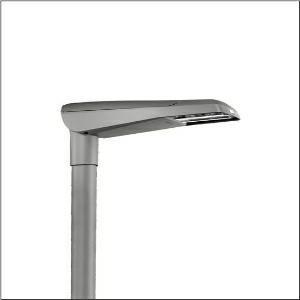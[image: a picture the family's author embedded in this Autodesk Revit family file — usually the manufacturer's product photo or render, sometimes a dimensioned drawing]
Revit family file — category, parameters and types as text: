
# Revit family: streetlight_sl_11_iq_micro___st1_2a_5xc1a51e08ce_3341
name_source: partatom
category: Lighting Fixtures
units: mm (PartAtom-declared; Revit-internal decimal feet)

## family parameters
Cut with Voids When Loaded = No
Host = Face
Light Source = No
Part Type = Normal
Room Calculation Point = No
Round Connector Dimension = Use Diameter
Shared = No

## types (1)
- --- (1 x LED, 1880 lm, 12.6 W, 3000K)
    Apparent Load = 13 VA
    CIE Flux Codes = 33 71 96 100 100
    Color Rendering = 70
    Color Temperature = 3000K
    Default Elevation = 1800 mm
    Description = Streetlight SL 11 iQ micro, mast luminaire, primary light control with 3 zone facetted reflector, of plastic, silver coated, highly specular, primary optical cover: cover, of PMMA, transparent, light distribution: ST1.2a, light emission: direct distribution, primary light characteristic: asymmetric, installation type: post-top, side-entry, lamps: LED, High Power LED, rated values: 1.880lm | 12,6W | 149,2lm/W (begin service life); end service life: 1.880lm | 12,9W; at 50% lumin. flux: 940lm | 6,8W | 138,2lm/W, colour temperature: 3000K, colour rendering: CRI > 70, light colour: 730, light setting 1 begin service life: 100% | 1.880lm | 12,6W | 149,2lm/W | 3.000K, light setting 1 end service life: 12,9W, further light settings possible, control: optimised constant luminous flux control (CLO 2.0), Desk-Remote (wireless, voltage-free reading and setting of iQ features in the workshop via application-optimized NFC function/RFID function), Light-Fading, Smart-Wire, Night-Set, Lumen-Switch, Temp-Guard, Auto-Match, with cable H07RN-F 3x 1.5mm², mains connection: 230..240V, AC, 50/60Hz, connection cable pre-assembled, cable length: 5,5m, luminaire housing, of diecast aluminium, powder-coated, SITECO metallic grey (DB 702S), please order mast flange separately, inclination adjustable without tools: 0°, 5°, 10°, 15° (post-top) | 0°, -5°, -10°, -15° (side-entry), sealing non-destructively replaceable, multi-level sealing system, length: 600mm, width: 174mm, height: 116mm, mast flange for spigot size: 42mm (side-entry): 5XC10008XM4, 60/48mm (side-entry/post-top): 5XC10108XM2, 76/60mm (side-entry/post-top): 5XC10108XM1, equipment: standard, protection rating (complete): IP66, insulation class (complete): insulation class II (safety insulation), certification: CE, ENEC, ENEC+, VDE, impact resistance: IK10, permissible operating ambient temperature for outdoor applications: -25..+50°C, standard-compliant lighting for roads and squares, Environmental Product Declaration (EPD) tested and certified by an independent institute, packaging unit: 1 piece

Light Distribution: ST1.2a
    Height = 116 mm
    Lamp = 1 x LED
    Lamp Light Flux = 1880 lm
    Lamp Power = 12.6 W
    Lamp count = 1
    Length = 600 mm
    Luminous efficacy = 149 lm/W
    Manufacturer = Siteco
    ModVariant = No
    Model = 5XC1A51E08CE
    Number of Poles = 1
    OnlyDefault = Yes
    Power Factor = 1
    Product Name = Streetlight SL 11 iQ micro | ST1.2a
    Product group = mast luminaire | pylon top
    ProductGroupID = 6100
    Protection Class = Protection class II
    Protection Degree = IP 66
    RLX_Detail_Level = 1
    RLX_Emergency_Light_Flux = 0 lm
    RLX_Emergency_Type = 0
    RLX_Emergency_Type_DB = No
    RlxData = <blob elided: 26533 chars, md5=75102967>
    Socket = socket
    Standby Power = 0 W
    System Light Flux = 1880 lm
    System Power = 13 W
    Type Comments = factory setting: luminous flux: 100 % | dim-lin: 254 | 229 mA
    Type Image = l_1006566.jpg
    URL = http://relux.com
    VarID = @adj_019141
    Voltage = 0 V
    Weight = 0.00 kg
    Width = 174 mm

## geometry (parser evidence)
native form markers: Blend x4, Sweep x12
no freeform markers — native parametric forms only
